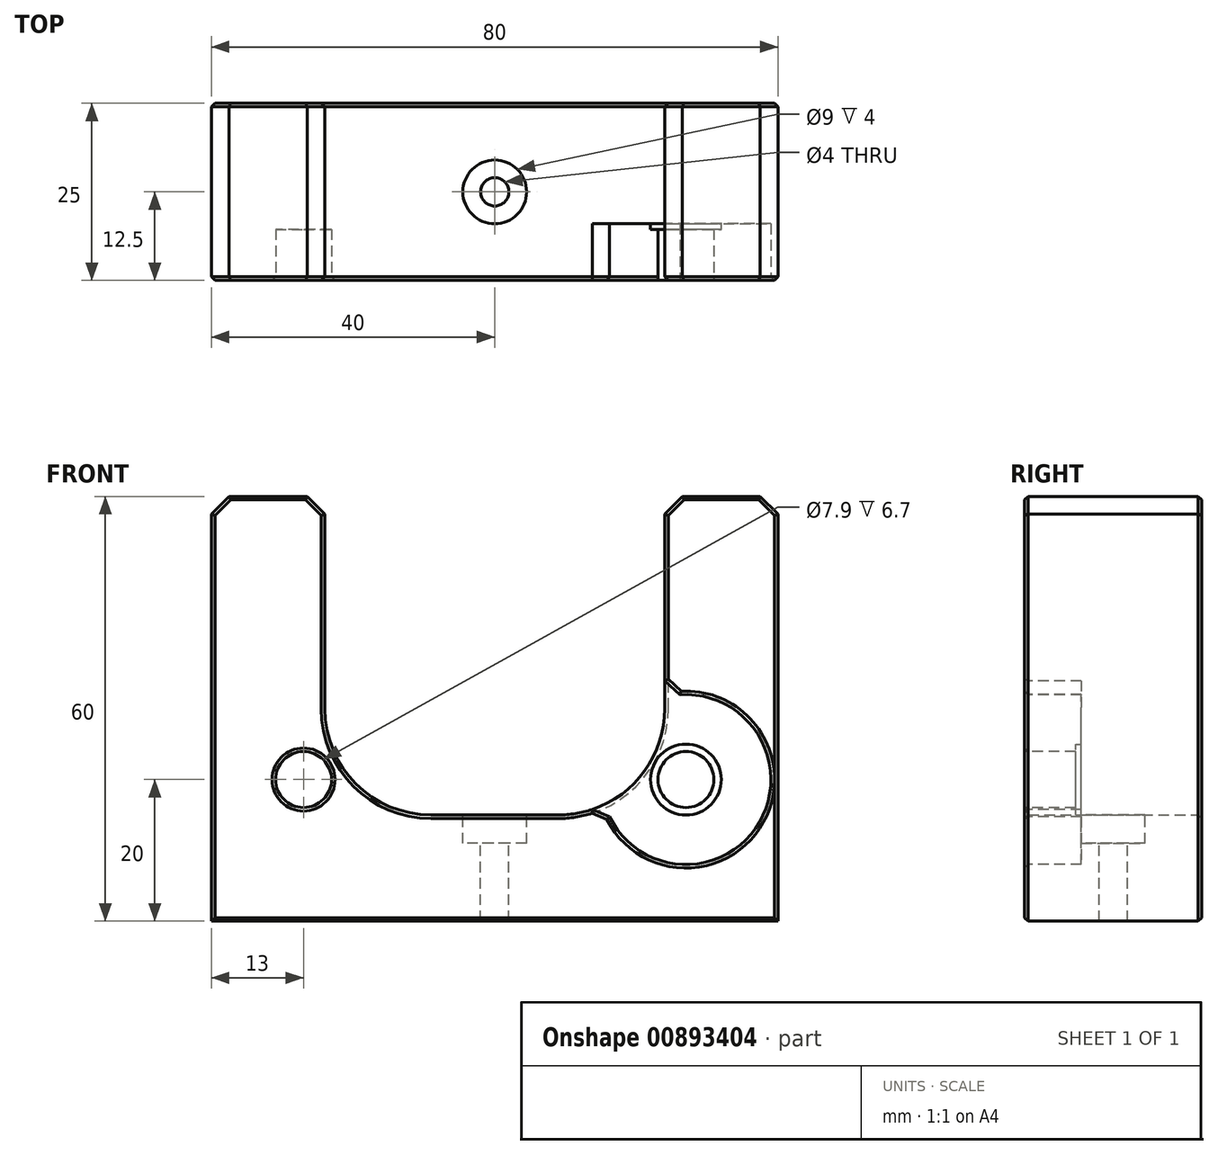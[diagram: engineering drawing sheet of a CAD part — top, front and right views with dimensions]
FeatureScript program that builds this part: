
annotation { "Feature Type Name" : "Feature", "Feature Type Description" : "" }
export const myFeature = defineFeature(function(context is Context, id is Id, definition is map)
    precondition{}
    {
        {
            var Q0;
            Q0=qCreatedBy(makeId("Front.planeOp"),FACE);
            var sketch = newSketch(context, id + "F0", { "sketchPlane" : qUnion([Q0])});
            skLineSegment(sketch, "E0.bottom", {"start": v(-40, 60) * mm, "end": v(-24, 60) * mm});
            skLineSegment(sketch, "E0.top", {"start": v(-40, 0) * mm, "end": v(40, 0) * mm});
            skLineSegment(sketch, "E0.left", {"start": v(-40, 60) * mm, "end": v(-40, 0) * mm});
            skLineSegment(sketch, "E0.right", {"start": v(40, 60) * mm, "end": v(40, 0) * mm});
            skLineSegment(sketch, "E1", {"start": v(-24, 60) * mm, "end": v(-24, 15) * mm});
            skLineSegment(sketch, "E2", {"start": v(-24, 15) * mm, "end": v(0, 15) * mm});
            skLineSegment(sketch, "E3", {"start": v(0, 74.86) * mm, "end": v(0, 66.34) * mm});
            skPoint(sketch, "E3.startSnap0", {"position": v(0, 60) * mm});
            skLineSegment(sketch, "E4.MirrorCS", {"start": v(24, 15) * mm, "end": v(0, 15) * mm});
            skLineSegment(sketch, "E5.MirrorCS", {"start": v(24, 60) * mm, "end": v(24, 15) * mm});
            skLineSegment(sketch, "E6.trimOffspring", {"start": v(24, 60) * mm, "end": v(40, 60) * mm});
            skSolve(sketch);
        }
        {
            var Q0;
            Q0=makeQuery(id+"F0.imprint","IMPRINT",FACE,{"disambiguationData":[TD([[makeQuery(id+"F0.imprint","IMPRINT",EDGE,{"derivedFrom":sQuery(id+"F0.wireOp",EDGE,"E0.bottom")}),-1.0]])]});
            extrude(context, id + "F1", {"entities" : qUnion([Q0]), "depth" : 25 * mm, "offsetDistance" : 25 * mm});
        }
        {
            var Q0;
            Q0=makeQuery(id+"F1.opExtrude","CAP_FACE",FACE,{"disambiguationData":[OSD([sQuery(id+"F0.wireOp",EDGE,"E0.bottom"),sQuery(id+"F0.wireOp",EDGE,"E0.top"),sQuery(id+"F0.wireOp",EDGE,"E0.left"),sQuery(id+"F0.wireOp",EDGE,"E0.right"),sQuery(id+"F0.wireOp",EDGE,"E1"),sQuery(id+"F0.wireOp",EDGE,"E2"),sQuery(id+"F0.wireOp",EDGE,"E4.MirrorCS"),sQuery(id+"F0.wireOp",EDGE,"E5.MirrorCS"),sQuery(id+"F0.wireOp",EDGE,"E6.trimOffspring")])],"isStart":false});
            var sketch = newSketch(context, id + "F2", { "sketchPlane" : qUnion([Q0])});
            skCircle(sketch, "E7", {"center": v(27, 20) * mm, "radius": 3.95 * mm});
            skLineSegment(sketch, "E8", {"start": v(0, 0) * mm, "end": v(0, 18.5) * mm});
            skCircle(sketch, "E9.MirrorC", {"center": v(-27, 20) * mm, "radius": 3.95 * mm});
            skCircle(sketch, "E10", {"center": v(-27, 20) * mm, "radius": 12 * mm});
            skCircle(sketch, "E11", {"center": v(27, 20) * mm, "radius": 12 * mm});
            skSolve(sketch);
        }
        {
            var Q0;
            Q0=makeQuery(id+"F1.opExtrude","SWEPT_EDGE",EDGE,{"disambiguationData":[OSD([sQuery(id+"F0.wireOp",EDGE,"E4.MirrorCS"),sQuery(id+"F0.wireOp",EDGE,"E5.MirrorCS")])]});
            var Q1;
            Q1=makeQuery(id+"F1.opExtrude","SWEPT_EDGE",EDGE,{"disambiguationData":[OSD([sQuery(id+"F0.wireOp",EDGE,"E1"),sQuery(id+"F0.wireOp",EDGE,"E2")])]});
            fillet(context, id + "F3", {"entities" : qUnion([Q0, Q1]), "radius" : 15 * mm, "tangentPropagation" : true, "allowEdgeOverflow" : false});
        }
        {
            var Q0;
            {var subQ1=makeQuery(id+"F1.opExtrude","CAP_EDGE",EDGE,{"disambiguationData":[OSD([sQuery(id+"F0.wireOp",EDGE,"E1")])],"isStart":false});var subQ5=sQuery(id+"F2.wireOp",EDGE,"E9.MirrorC");var subQ6=makeQuery(id+"F2.imprint","INTERSECT",VERTEX,{"disambiguationData":[OD(0.0)],"derivedFrom":[subQ1,subQ5]});Q0=makeQuery(id+"F2.imprint","IMPRINT",FACE,{"disambiguationData":[TD([[makeQuery(id+"F2.imprint","IMPRINT",EDGE,{"disambiguationData":[TD([[subQ6,-1.0]])],"derivedFrom":subQ5}),1.0]])]});}
            var Q1;
            {var subQ1=makeQuery(id+"F1.opExtrude","CAP_EDGE",EDGE,{"disambiguationData":[OSD([sQuery(id+"F0.wireOp",EDGE,"E1")])],"isStart":false});var subQ6=sQuery(id+"F2.wireOp",EDGE,"E9.MirrorC");var subQ7=makeQuery(id+"F2.imprint","INTERSECT",VERTEX,{"disambiguationData":[OD(0.0)],"derivedFrom":[subQ1,subQ6]});Q1=makeQuery(id+"F2.imprint","IMPRINT",FACE,{"disambiguationData":[TD([[makeQuery(id+"F2.imprint","IMPRINT",EDGE,{"disambiguationData":[TD([[subQ7,1.0]])],"derivedFrom":subQ6}),1.0]])]});}
            var Q2;
            {var subQ0=makeQuery(id+"F1.opExtrude","CAP_EDGE",EDGE,{"disambiguationData":[OSD([sQuery(id+"F0.wireOp",EDGE,"E5.MirrorCS")])],"isStart":false});var subQ3=sQuery(id+"F2.wireOp",EDGE,"E7");var subQ4=makeQuery(id+"F2.imprint","INTERSECT",VERTEX,{"disambiguationData":[OD(0.0)],"derivedFrom":[subQ0,subQ3]});Q2=makeQuery(id+"F2.imprint","IMPRINT",FACE,{"disambiguationData":[TD([[makeQuery(id+"F2.imprint","IMPRINT",EDGE,{"disambiguationData":[TD([[subQ4,-1.0]])],"derivedFrom":subQ3}),-1.0]])]});}
            var Q3;
            {var subQ0=makeQuery(id+"F1.opExtrude","CAP_EDGE",EDGE,{"disambiguationData":[OSD([sQuery(id+"F0.wireOp",EDGE,"E5.MirrorCS")])],"isStart":false});var subQ6=sQuery(id+"F2.wireOp",EDGE,"E7");var subQ7=makeQuery(id+"F2.imprint","INTERSECT",VERTEX,{"disambiguationData":[OD(0.0)],"derivedFrom":[subQ0,subQ6]});Q3=makeQuery(id+"F2.imprint","IMPRINT",FACE,{"disambiguationData":[TD([[makeQuery(id+"F2.imprint","IMPRINT",EDGE,{"disambiguationData":[TD([[subQ7,1.0]])],"derivedFrom":subQ6}),-1.0]])]});}
            extrude(context, id + "F4", {"entities" : qUnion([Q0, Q1, Q2, Q3]), "operationType" : NewBodyOperationType.REMOVE, "oppositeDirection" : true, "depth" : 8 * mm, "offsetDistance" : 25 * mm});
        }
        {
            var Q0;
            Q0=makeQuery(id+"F4.boolean.opBoolean","COPY",FACE,{"derivedFrom":makeQuery(id+"F4.opExtrude","CAP_FACE",FACE,{"disambiguationData":[OSD([sQuery(id+"F2.wireOp",EDGE,"E9.MirrorC"),sQuery(id+"F2.wireOp",EDGE,"E10")])],"isStart":false})});
            var sketch = newSketch(context, id + "F5", { "sketchPlane" : qUnion([Q0])});
            skCircle(sketch, "E12", {"center": v(-27, 20) * mm, "radius": 5 * mm});
            skLineSegment(sketch, "E13", {"start": v(0, 0.7) * mm, "end": v(0, 20.28) * mm});
            skCircle(sketch, "E14.MirrorC", {"center": v(27, 20) * mm, "radius": 5 * mm});
            skSolve(sketch);
        }
        {
            var Q0;
            Q0 = qSketchRegion(id + "F5", true);
            extrude(context, id + "F6", {"entities" : qUnion([Q0]), "operationType" : NewBodyOperationType.ADD, "depth" : 0.8 * mm, "offsetDistance" : 25 * mm});
        }
        {
            var Q0;
            Q0=makeQuery(id+"F1.opExtrude","SWEPT_EDGE",EDGE,{"disambiguationData":[OSD([sQuery(id+"F0.wireOp",EDGE,"E0.bottom"),sQuery(id+"F0.wireOp",EDGE,"E0.left")])]});
            var Q1;
            Q1=makeQuery(id+"F1.opExtrude","SWEPT_EDGE",EDGE,{"disambiguationData":[OSD([sQuery(id+"F0.wireOp",EDGE,"E0.bottom"),sQuery(id+"F0.wireOp",EDGE,"E1")])]});
            var Q2;
            Q2=makeQuery(id+"F1.opExtrude","SWEPT_EDGE",EDGE,{"disambiguationData":[OSD([sQuery(id+"F0.wireOp",EDGE,"E5.MirrorCS"),sQuery(id+"F0.wireOp",EDGE,"E6.trimOffspring")])]});
            var Q3;
            Q3=makeQuery(id+"F1.opExtrude","SWEPT_EDGE",EDGE,{"disambiguationData":[OSD([sQuery(id+"F0.wireOp",EDGE,"E0.right"),sQuery(id+"F0.wireOp",EDGE,"E6.trimOffspring")])]});
            chamfer(context, id + "F7", {"entities" : qUnion([Q0, Q1, Q2, Q3]), "width" : 2.5 * mm, "tangentPropagation" : true});
        }
        {
            var Q0;
            Q0=makeQuery(id+"F4.boolean.opBoolean","INTERSECT",EDGE,{"derivedFrom":[makeQuery(id+"F1.opExtrude","SWEPT_FACE",FACE,{"disambiguationData":[OSD([sQuery(id+"F0.wireOp",EDGE,"E1")])]}),makeQuery(id+"F4.opExtrude","SWEPT_FACE",FACE,{"disambiguationData":[OSD([sQuery(id+"F2.wireOp",EDGE,"E10")])]})]});
            var Q1;
            Q1=makeQuery(id+"F4.boolean.opBoolean","INTERSECT",EDGE,{"derivedFrom":[makeQuery(id+"F3.opFillet","BLEND_FACE",FACE,{"disambiguationData":[OSD([sQuery(id+"F0.wireOp",EDGE,"E1"),sQuery(id+"F0.wireOp",EDGE,"E2")])]}),makeQuery(id+"F4.opExtrude","SWEPT_FACE",FACE,{"disambiguationData":[OSD([sQuery(id+"F2.wireOp",EDGE,"E10")])]})]});
            var Q2;
            Q2=makeQuery(id+"F4.boolean.opBoolean","INTERSECT",EDGE,{"derivedFrom":[makeQuery(id+"F3.opFillet","BLEND_FACE",FACE,{"disambiguationData":[OSD([sQuery(id+"F0.wireOp",EDGE,"E4.MirrorCS"),sQuery(id+"F0.wireOp",EDGE,"E5.MirrorCS")])]}),makeQuery(id+"F4.opExtrude","SWEPT_FACE",FACE,{"disambiguationData":[OSD([sQuery(id+"F2.wireOp",EDGE,"E11")])]})]});
            var Q3;
            Q3=makeQuery(id+"F4.boolean.opBoolean","INTERSECT",EDGE,{"derivedFrom":[makeQuery(id+"F1.opExtrude","SWEPT_FACE",FACE,{"disambiguationData":[OSD([sQuery(id+"F0.wireOp",EDGE,"E5.MirrorCS")])]}),makeQuery(id+"F4.opExtrude","SWEPT_FACE",FACE,{"disambiguationData":[OSD([sQuery(id+"F2.wireOp",EDGE,"E11")])]})]});
            chamfer(context, id + "F8", {"entities" : qUnion([Q0, Q1, Q2, Q3]), "width" : 2 * mm, "tangentPropagation" : true});
        }
        {
            var Q0;
            {var subQ0=sQuery(id+"F0.wireOp",EDGE,"E5.MirrorCS");var subQ1=sQuery(id+"F0.wireOp",EDGE,"E4.MirrorCS");var subQ2=sQuery(id+"F0.wireOp",EDGE,"E0.right");var subQ3=sQuery(id+"F0.wireOp",EDGE,"E2");var subQ4=sQuery(id+"F0.wireOp",EDGE,"E1");var subQ5=sQuery(id+"F0.wireOp",EDGE,"E0.left");var subQ6=sQuery(id+"F0.wireOp",EDGE,"E6.trimOffspring");var subQ7=sQuery(id+"F0.wireOp",EDGE,"E0.bottom");var subQ8=sQuery(id+"F0.wireOp",EDGE,"E0.top");Q0=makeQuery(id+"F4.boolean.opBoolean","SPLIT",FACE,{"disambiguationData":[TD([makeQuery(id+"F1.opExtrude","SWEPT_FACE",FACE,{"disambiguationData":[OSD([subQ7])]})])],"derivedFrom":makeQuery(id+"F1.opExtrude","CAP_FACE",FACE,{"disambiguationData":[OSD([subQ7,subQ8,subQ5,subQ2,subQ4,subQ3,subQ1,subQ0,subQ6])],"isStart":false})});}
            var Q1;
            Q1=makeQuery(id+"F1.opExtrude","CAP_FACE",FACE,{"disambiguationData":[OSD([sQuery(id+"F0.wireOp",EDGE,"E0.bottom"),sQuery(id+"F0.wireOp",EDGE,"E0.top"),sQuery(id+"F0.wireOp",EDGE,"E0.left"),sQuery(id+"F0.wireOp",EDGE,"E0.right"),sQuery(id+"F0.wireOp",EDGE,"E1"),sQuery(id+"F0.wireOp",EDGE,"E2"),sQuery(id+"F0.wireOp",EDGE,"E4.MirrorCS"),sQuery(id+"F0.wireOp",EDGE,"E5.MirrorCS"),sQuery(id+"F0.wireOp",EDGE,"E6.trimOffspring")])],"isStart":true});
            chamfer(context, id + "F9", {"entities" : qUnion([Q0, Q1]), "width" : 0.5 * mm, "tangentPropagation" : true});
        }
        {
            var Q0;
            Q0=makeQuery(id+"F1.opExtrude","SWEPT_FACE",FACE,{"disambiguationData":[OSD([sQuery(id+"F0.wireOp",EDGE,"E2"),sQuery(id+"F0.wireOp",EDGE,"E4.MirrorCS")])]});
            var sketch = newSketch(context, id + "F10", { "sketchPlane" : qUnion([Q0])});
            skCircle(sketch, "E15", {"center": v(0, -12.5) * mm, "radius": 4.5 * mm});
            skCircle(sketch, "E16", {"center": v(0, -12.5) * mm, "radius": 2 * mm});
            skSolve(sketch);
        }
        {
            var Q0;
            Q0=makeQuery(id+"F10.imprint","IMPRINT",FACE,{"disambiguationData":[TD([[makeQuery(id+"F10.imprint","IMPRINT",EDGE,{"derivedFrom":sQuery(id+"F10.wireOp",EDGE,"E15")}),1.0]])]});
            extrude(context, id + "F11", {"entities" : qUnion([Q0]), "operationType" : NewBodyOperationType.REMOVE, "oppositeDirection" : true, "depth" : 4 * mm, "offsetDistance" : 25 * mm});
        }
        {
            var Q0;
            Q0=makeQuery(id+"F11.boolean.opBoolean","SPLIT",FACE,{"disambiguationData":[TD([makeQuery(id+"F11.opExtrude","SWEPT_FACE",FACE,{"disambiguationData":[OSD([sQuery(id+"F10.wireOp",EDGE,"E16")])]})])],"derivedFrom":makeQuery(id+"F1.opExtrude","SWEPT_FACE",FACE,{"disambiguationData":[OSD([sQuery(id+"F0.wireOp",EDGE,"E2"),sQuery(id+"F0.wireOp",EDGE,"E4.MirrorCS")])]})});
            extrude(context, id + "F12", {"entities" : qUnion([Q0]), "operationType" : NewBodyOperationType.REMOVE, "oppositeDirection" : true, "depth" : 25 * mm, "offsetDistance" : 25 * mm});
        }
    });
